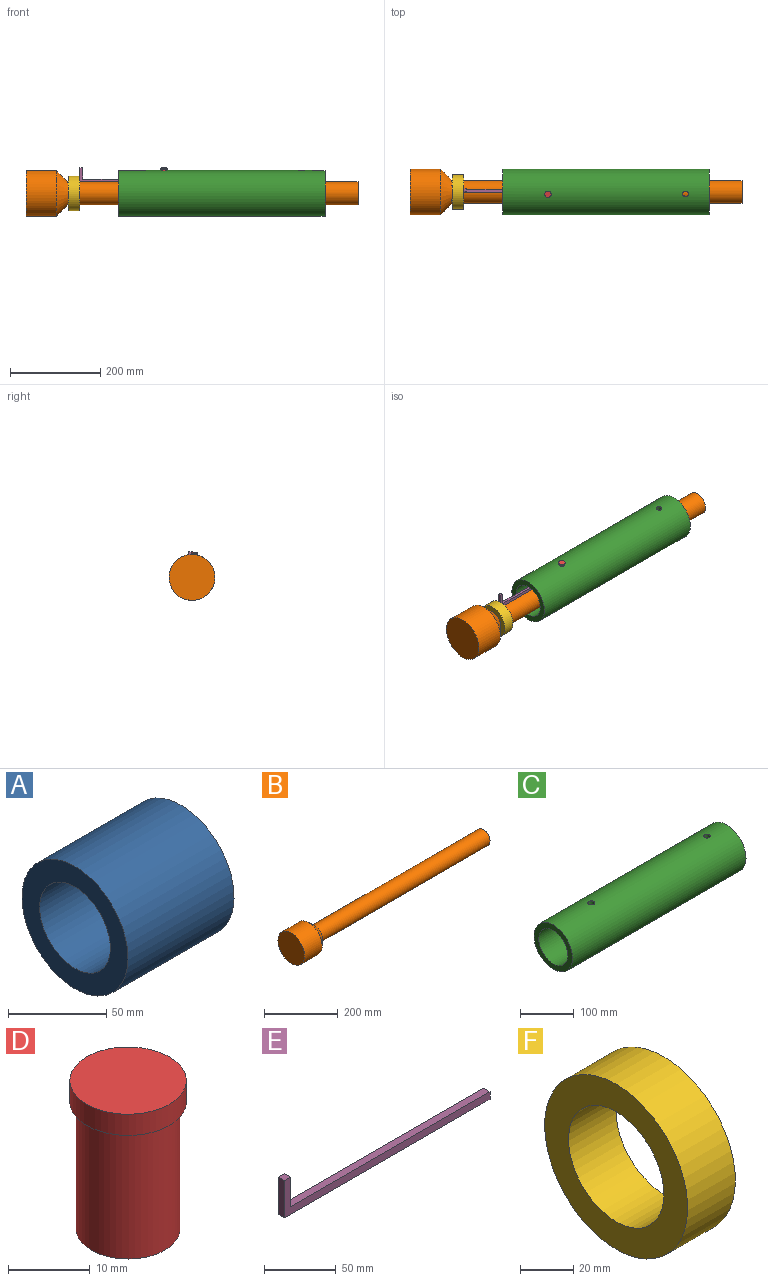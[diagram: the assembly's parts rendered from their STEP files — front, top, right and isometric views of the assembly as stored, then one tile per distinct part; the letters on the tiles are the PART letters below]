
ASSEMBLY  parts=6 mates=4
PART A: 4 faces, bbox 76.2x76.2x76.2 mm
  f0: plane 76.2x76.2mm, normal (-1,0,0), area 2533.5mm2, adj f1,f3
  f1: cylinder r=25.4mm len=76.2mm, axis (-1,0,0), area 12161mm2, adj f0,f2
  f2: plane 76.2x76.2mm, normal (1,0,0), area 2533.5mm2, adj f1,f3
  f3: cylinder r=38.1mm len=76.2mm, axis (-1,0,0), area 18241.5mm2, adj f0,f2
PART B: 5 faces, bbox 735.3x101.6x101.6 mm
  f0: cylinder r=25.4mm len=642.7mm, axis (1,0,0), area 102569.9mm2, adj f1,f4
  f1: cone r=50.8mm half-angle=45deg, axis (-1,0,0), area 8599.1mm2, adj f0,f2
  f2: cylinder r=50.8mm len=101.6mm, axis (1,0,0), area 21465.9mm2, adj f1,f3
  f3: plane 101.6x101.6mm, normal (-1,0,0), area 8107.3mm2, adj f2
  f4: plane 50.8x50.8mm, normal (1,0,0), area 2026.8mm2, adj f0
PART C: 6 faces, bbox 457.2x101.6x101.6 mm
  f0: cylinder r=38.1mm len=457.2mm, axis (-1,0,0), area 109200.5mm2, adj f2,f3,f4,f5
  f1: cylinder r=50.8mm len=457.2mm, axis (-1,0,0), area 145683.5mm2, adj f2,f3,f4,f5
  f2: plane 101.6x101.6mm, normal (-1,0,0), area 3547mm2, adj f0,f1
  f3: plane 101.6x101.6mm, normal (1,0,0), area 3547mm2, adj f0,f1
  f4: cylinder r=6.21mm len=13.21mm, axis (0,0,-1), area 497.8mm2, adj f0,f1
  f5: cylinder r=6.35mm len=13.23mm, axis (0,0,-1), area 509.4mm2, adj f0,f1
PART D: 5 faces, bbox 14.2x14.2x22.2 mm
  f0: cylinder r=6.35mm len=19.05mm, axis (0,0,-1), area 760.1mm2, adj f1,f4
  f1: plane 12.7x12.7mm, normal (0,0,-1), area 126.7mm2, adj f0
  f2: cylinder r=7.12mm len=14.24mm, axis (0,0,-1), area 142.1mm2, adj f3,f4
  f3: plane 14.24x14.24mm, normal (0,0,1), area 159.3mm2, adj f2
  f4: plane 14.24x14.24mm, normal (0,0,-1), area 32.7mm2, adj f0,f2
PART E: 8 faces, bbox 203.2x6.4x31.8 mm
  f0: plane 203.2x6.35mm, normal (0,0,-1), area 1290.3mm2, adj f1,f5,f6,f7
  f1: plane 6.35x6.35mm, normal (1,0,0), area 40.3mm2, adj f0,f2,f6,f7
  f2: plane 196.85x6.35mm, normal (0,0,1), area 1250mm2, adj f1,f3,f6,f7
  f3: plane 25.4x6.35mm, normal (1,0,0), area 161.3mm2, adj f2,f4,f6,f7
  f4: plane 6.35x6.35mm, normal (0,0,1), area 40.3mm2, adj f3,f5,f6,f7
  f5: plane 31.75x6.35mm, normal (-1,0,0), area 201.6mm2, adj f0,f4,f6,f7
  f6: plane 203.2x31.75mm, normal (0,-1,0), area 1451.6mm2, adj f0,f1,f2,f3,f4,f5
  f7: plane 203.2x31.75mm, normal (0,1,0), area 1451.6mm2, adj f0,f1,f2,f3,f4,f5
PART F: 4 faces, bbox 25.4x76.2x76.2 mm
  f0: plane 76.2x76.2mm, normal (-1,0,0), area 2533.5mm2, adj f1,f3
  f1: cylinder r=25.4mm len=50.8mm, axis (-1,0,0), area 4053.7mm2, adj f0,f2
  f2: plane 76.2x76.2mm, normal (1,0,0), area 2533.5mm2, adj f1,f3
  f3: cylinder r=38.1mm len=76.2mm, axis (-1,0,0), area 6080.5mm2, adj f0,f2
PLACE A rot(axis=(1,0,0),57.5deg) t=(80.12,9.03,-11.64)mm fixed
PLACE B rot(axis=(-1,0,0),57.2deg) t=(-160.11,9.03,-11.64)mm
PLACE C rot(axis=(1,0,0),5.4deg) t=(154.78,9.03,-11.64)mm
PLACE D rot(axis=(0.03,-0.05,1),110.1deg) t=(2.38,5.8,22.27)mm
PLACE E rot(axis=(-1,0,0),3.4deg) t=(-82.02,11.79,16.78)mm
PLACE F rot(axis=(1,0,0),99.6deg) t=(-193.92,9.03,-11.64)mm
MATE cylindrical B.f0 <-> A.f1  axis (1,0,0) through (432.23,9.03,-11.64)mm
MATE planar E.f5 <-> F.f1  axis (-1,0,0) through (-183.62,11.6,13.61)mm
MATE cylindrical C.f0 <-> B.f0  axis (-1,0,0) through (130.55,9.03,-11.64)mm
MATE cylindrical D.f0 <-> C.f5  axis (0,0.09,-1) through (2.38,5.8,22.27)mm
